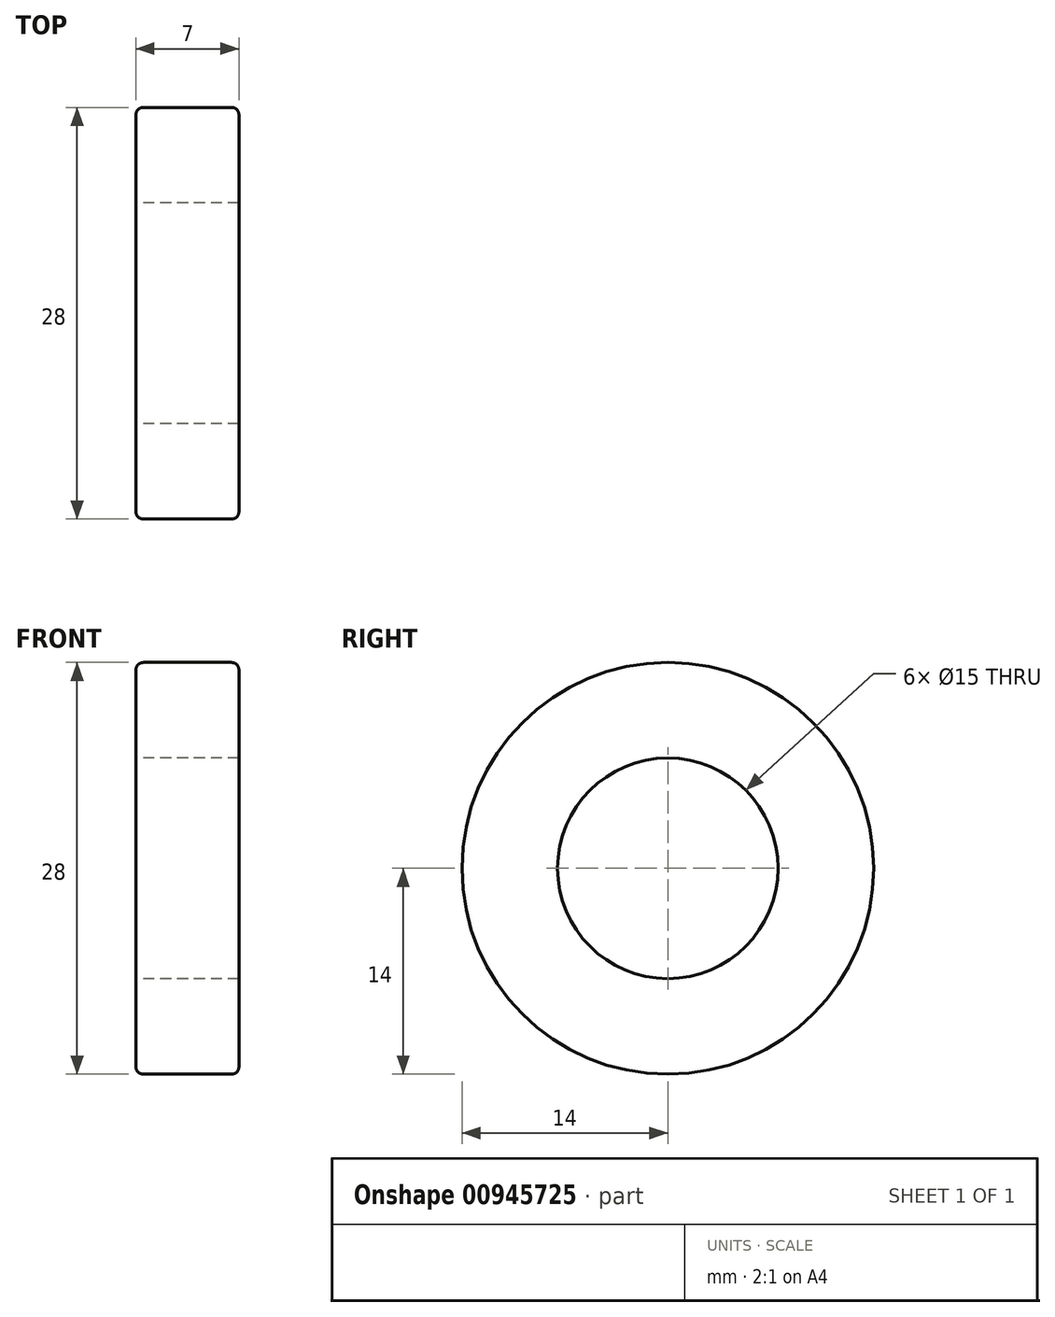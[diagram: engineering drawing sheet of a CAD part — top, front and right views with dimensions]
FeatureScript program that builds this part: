
annotation { "Feature Type Name" : "Feature", "Feature Type Description" : "" }
export const myFeature = defineFeature(function(context is Context, id is Id, definition is map)
    precondition{}
    {
        {
            var Q0;
            Q0=qCreatedBy(makeId("Front.planeOp"),FACE);
            var sketch = newSketch(context, id + "F0", { "sketchPlane" : qUnion([Q0])});
            skLineSegment(sketch, "E0", {"start": v(0, 7.5) * mm, "end": v(7, 7.5) * mm});
            skLineSegment(sketch, "E1", {"start": v(7, 7.5) * mm, "end": v(7, 13.5) * mm});
            skLineSegment(sketch, "E2", {"start": v(6.5, 14) * mm, "end": v(0.5, 14) * mm});
            skLineSegment(sketch, "E3", {"start": v(0, 13.5) * mm, "end": v(0, 7.5) * mm});
            skLineSegment(sketch, "E4", {"start": v(0, 0) * mm, "end": v(13.28, 0) * mm});
            skArc(sketch, "E5", {"start": v(0.5, 14) * mm, "mid": v(0.15, 13.85) * mm, "end": v(0, 13.5) * mm});
            skPoint(sketch, "E6.orphan", {"position": v(0, 14) * mm});
            skArc(sketch, "E7.MirrorCS", {"start": v(6.5, 14) * mm, "mid": v(6.85, 13.85) * mm, "end": v(7, 13.5) * mm});
            skSolve(sketch);
        }
        {
            var Q0;
            Q0=makeQuery(id+"F0.imprint","IMPRINT",FACE,{"disambiguationData":[TD([[makeQuery(id+"F0.imprint","IMPRINT",EDGE,{"derivedFrom":sQuery(id+"F0.wireOp",EDGE,"E0")}),1.0]])]});
            var Q1;
            Q1=sQuery(id+"F0.wireOp",EDGE,"E4");
            revolve(context, id + "F1", {"surfaceOperationType" : NewSurfaceOperationType.NEW, "entities" : qUnion([Q0]), "axis" : qUnion([Q1]), "revolveType" : RevolveType.FULL});
        }
    });
